# Revit family: Faucet-Lavatory-Grohe-Essence_New-23486_Series
name_source: partatom
category: Plumbing Fixtures
revit_build: Autodesk Revit 2018 (Build: 20170223_1515(x64)
units: mm (PartAtom-declared; Revit-internal decimal feet)

## family parameters
Always vertical = No
Cut with Voids When Loaded = No
OmniClass Number = 23.45.55.14
OmniClass Title = Single Faucets
Part Type = Normal
Room Calculation Point = No
Round Connector Dimension = Use Diameter
Shared = Yes
Work Plane-Based = Yes

## types (5) — shared parameters
ADA Compliant = Yes
Assembly Code = D2020300
CW Connection = Yes
CWFU = 1.5
Cold Water Connection Diameter = 3/8"
Cold Water Connection Radius = 3/16"
Default Elevation = 0"
Description = Essence New Single Hole Single-Handle L-Size Bathroom Faucet 1.2 GPM
Flow Rate = 1.2 gpm (4.56 L/min)
HW Connection = Yes
HWFU = 1.5
Height = 9 5/8"
Hot Water Connection Diameter = 0"
Hot Water Connection Radius = 3/16"
IAPMO Compliance = NSF 61, ASME A112.18.1/CSA B125.1,ICC/ANSI A117.1
Installation Type = Deck-Mounted
Length = 5"
Manufacturer = Grohe
Price = Prices may vary. Please consult Manufacturer Representative for most up-to-date price list.
Product Documentation Link = https://americanstandard.box.com
Product Page URL = https://www.grohe.us
Revised Date = 05/28/2021
URL = https://www.grohe.us
Vent Connection = No
Warranty Documentation Link = https://cdn.cloud.grohe.com
Waste Connection = No
cUPC Compliant = Yes
zero-valued in all types: WFU

## per-type parameters (varying)
| type | Finish | Material |
| 2348600A | Brass-Grohe-00A-StarLight Chrome | Brass-Grohe-00A-StarLight Chrome |
| 23486A0A | Brass-Grohe-A0A-Hard Graphite | Brass-Grohe-A0A-Hard Graphite |
| 23486BEA | Brass-Grohe-BEA-Polished Nickel Infinity Finish | Brass-Grohe-BEA-Polished Nickel Infinity Finish |
| 23486ENA | Brass-Grohe-ENA-Brushed Nickel Infinity Finish | Brass-Grohe-ENA-Brushed Nickel Infinity Finish |
| 23486GNA | Brass-Grohe-GNA-Brushed Cool Sunrise | Brass-Grohe-GNA-Brushed Cool Sunrise |

note: column(s) folded — value = type name in every type: Model

## geometry (parser evidence)
native form markers: Sweep x2
no freeform markers — native parametric forms only
